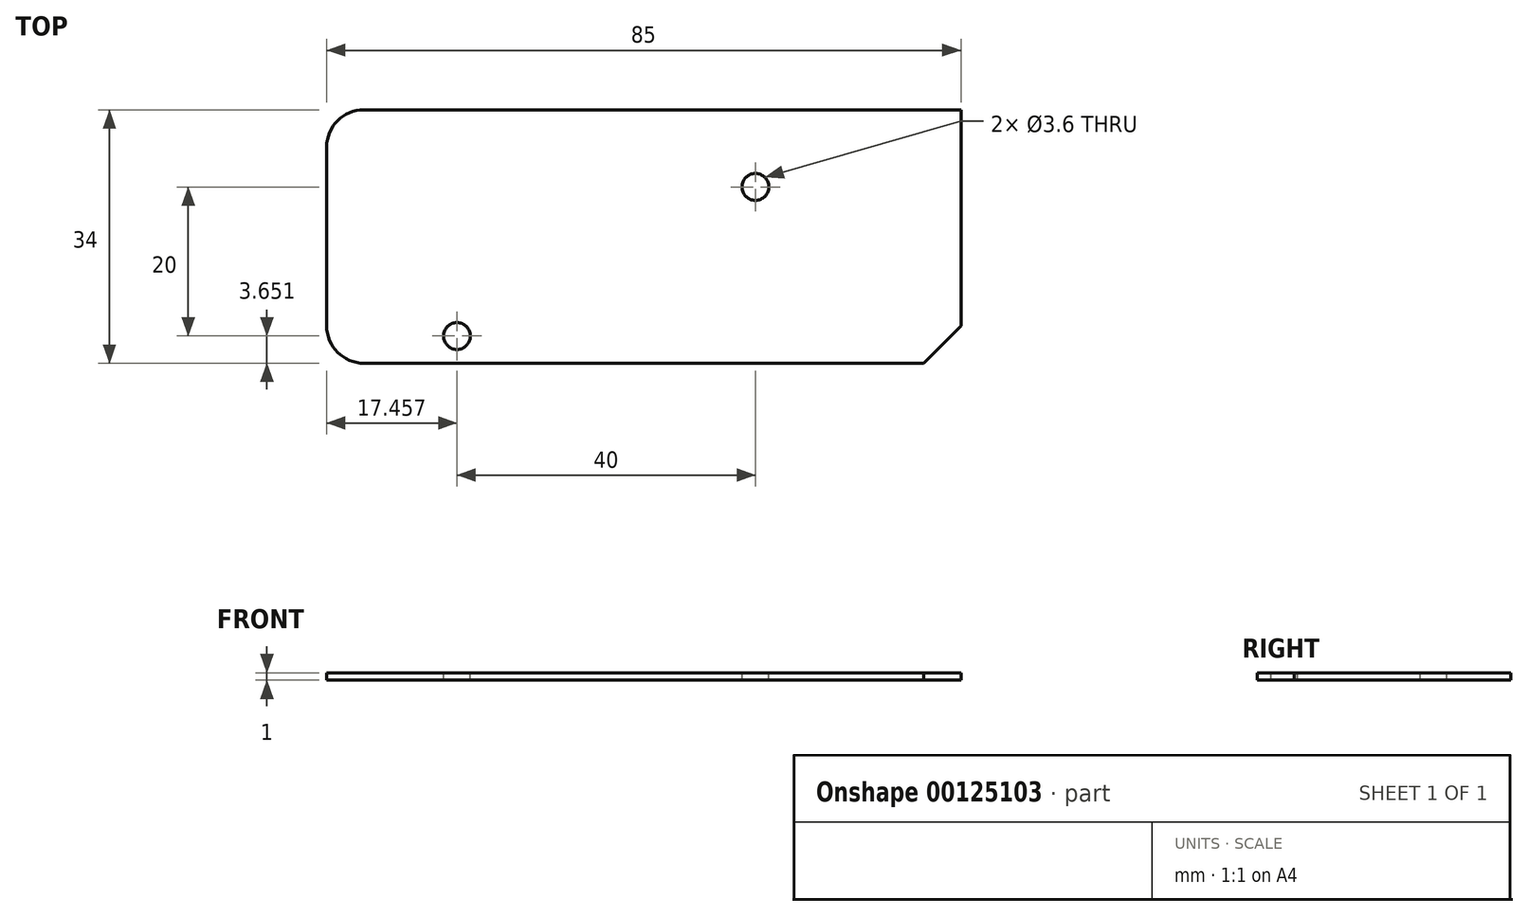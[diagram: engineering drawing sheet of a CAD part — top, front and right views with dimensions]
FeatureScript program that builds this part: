
annotation { "Feature Type Name" : "Feature", "Feature Type Description" : "" }
export const myFeature = defineFeature(function(context is Context, id is Id, definition is map)
    precondition{}
    {
        {
            var Q0;
            Q0=qCreatedBy(makeId("Top.planeOp"),FACE);
            var sketch = newSketch(context, id + "F0", { "sketchPlane" : qUnion([Q0])});
            skLineSegment(sketch, "E0.bottom", {"start": v(41.92, 16.36) * mm, "end": v(-38.08, 16.36) * mm});
            skLineSegment(sketch, "E0.top", {"start": v(41.92, -17.64) * mm, "end": v(-38.08, -17.64) * mm});
            skLineSegment(sketch, "E0.left", {"start": v(41.92, 16.36) * mm, "end": v(41.92, -17.64) * mm});
            skLineSegment(sketch, "E0.right", {"start": v(-43.08, 11.36) * mm, "end": v(-43.08, -12.64) * mm});
            skPoint(sketch, "E1.visualSharp", {"position": v(-43.08, -17.64) * mm});
            skArc(sketch, "E1.filletArc", {"start": v(-43.08, -12.64) * mm, "mid": v(-41.62, -16.17) * mm, "end": v(-38.08, -17.64) * mm});
            skPoint(sketch, "E2.visualSharp", {"position": v(-43.08, 16.36) * mm});
            skArc(sketch, "E2.filletArc", {"start": v(-38.08, 16.36) * mm, "mid": v(-41.62, 14.9) * mm, "end": v(-43.08, 11.36) * mm});
            skSolve(sketch);
        }
        {
            var Q0;
            Q0=makeQuery(id+"F0.imprint","IMPRINT",FACE,{"disambiguationData":[TD([[makeQuery(id+"F0.imprint","IMPRINT",EDGE,{"derivedFrom":sQuery(id+"F0.wireOp",EDGE,"E0.bottom")}),1.0]])]});
            extrude(context, id + "F1", {"entities" : qUnion([Q0]), "depth" : 1 * mm});
        }
        {
            var Q0;
            Q0=qCreatedBy(makeId("Top.planeOp"),FACE);
            var sketch = newSketch(context, id + "F2", { "sketchPlane" : qUnion([Q0])});
            skPoint(sketch, "E3", {"position": v(-25.62, -13.99) * mm});
            skPoint(sketch, "E4", {"position": v(14.38, 6.01) * mm});
            skSolve(sketch);
        }
        {
            var Q0;
            Q0=sQuery(id+"F2.wireOp",VERTEX,"E3");
            var Q1;
            Q1=sQuery(id+"F2.wireOp",VERTEX,"E4");
            var Q2;
            Q2=makeQuery(id+"F1.opExtrude","SWEPT_BODY",BODY,{"disambiguationData":[OSD([sQuery(id+"F0.wireOp",EDGE,"E0.bottom"),sQuery(id+"F0.wireOp",EDGE,"E0.top"),sQuery(id+"F0.wireOp",EDGE,"E0.left"),sQuery(id+"F0.wireOp",EDGE,"E0.right"),sQuery(id+"F0.wireOp",EDGE,"E1.filletArc"),sQuery(id+"F0.wireOp",EDGE,"E2.filletArc")])]});
            hole(context, id + "F3", {"style" : HoleStyle.SIMPLE, "endStyle" : HoleEndStyle.THROUGH, "oppositeDirection" : true, "holeDiameter" : 3.6 * mm, "locations" : qUnion([Q0, Q1]), "scope" : qUnion([Q2]), "isTappedThrough" : true});
        }
        {
            var Q0;
            Q0=makeQuery(id+"F1.opExtrude","SWEPT_EDGE",EDGE,{"disambiguationData":[OSD([sQuery(id+"F0.wireOp",EDGE,"E0.top"),sQuery(id+"F0.wireOp",EDGE,"E0.left")])]});
            chamfer(context, id + "F4", {"entities" : qUnion([Q0]), "width" : 5 * mm, "tangentPropagation" : true});
        }
    });
